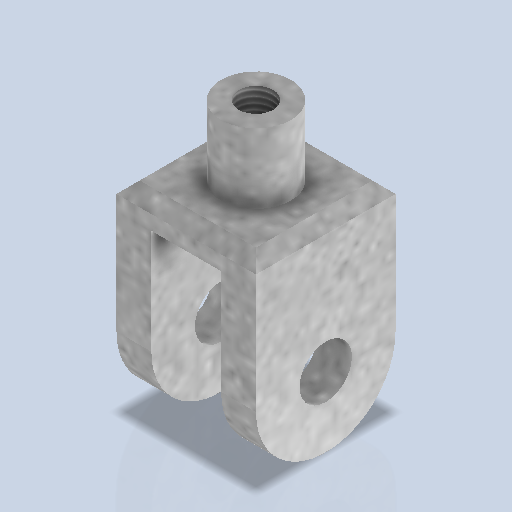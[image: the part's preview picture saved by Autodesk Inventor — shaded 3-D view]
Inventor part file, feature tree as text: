
AUTODESK INVENTOR PART (.ipt)
format: ipt  version: 2024.2 (Build 282272000, 272)  size: 293,376 bytes
history: native  units: mm
features: sketch x4, extrude x2, fillet x2, hole x2, chamfer x1
ambient origin geometry x8: Origin, YZ Plane, XZ Plane, XY Plane, X Axis, Y Axis, Z Axis, Center Point
bodies: Volumenkörper1 (feature_tree)
feature tree (11):
  extrude  "Extrusion1"  Depth=6.0mm
  fillet  "Rundung1"  Radius=12.0mm
  fillet  "Rundung2"  Radius=30.0mm
  hole  "Bohrung1"  [1 undecoded]
  chamfer  "Fasen1"  Distance=2.0mm Angle=45.0deg
  extrude  "Extrusion2"  Depth=12.0mm
  hole  "Bohrung2"  [1 undecoded]
  sketch  "Skizze1"  dims[d0=6.0mm d1=6.0mm d2=12.0mm d3=30.0mm]
  sketch  "Skizze2"  dims[d4=4.5mm d5=24.0mm d6=0.0mm]
  sketch  "Skizze3"  dims[d7=12.0mm]
  sketch  "Skizze4"  dims[d8=12.0mm d9=9.0mm d10=6.0mm d11=4.0mm d12=2.0mm d13=90.0deg d14=8.0mm d15=20.594885mm d16=2.0mm d17=2.0mm d18=45.0deg d19=12.0mm d20=12.0mm d21=0.0mm d22=5.917468mm d23=14.0mm d24=4.0mm d25=2.0mm d26=90.0deg d27=16.5mm d28=20.594885mm]
note: 2 required parameter values undecoded (feature->parameter linkage not recoverable at this tier; creation-order binding heuristic only, values carry confidence <= 0.55)
